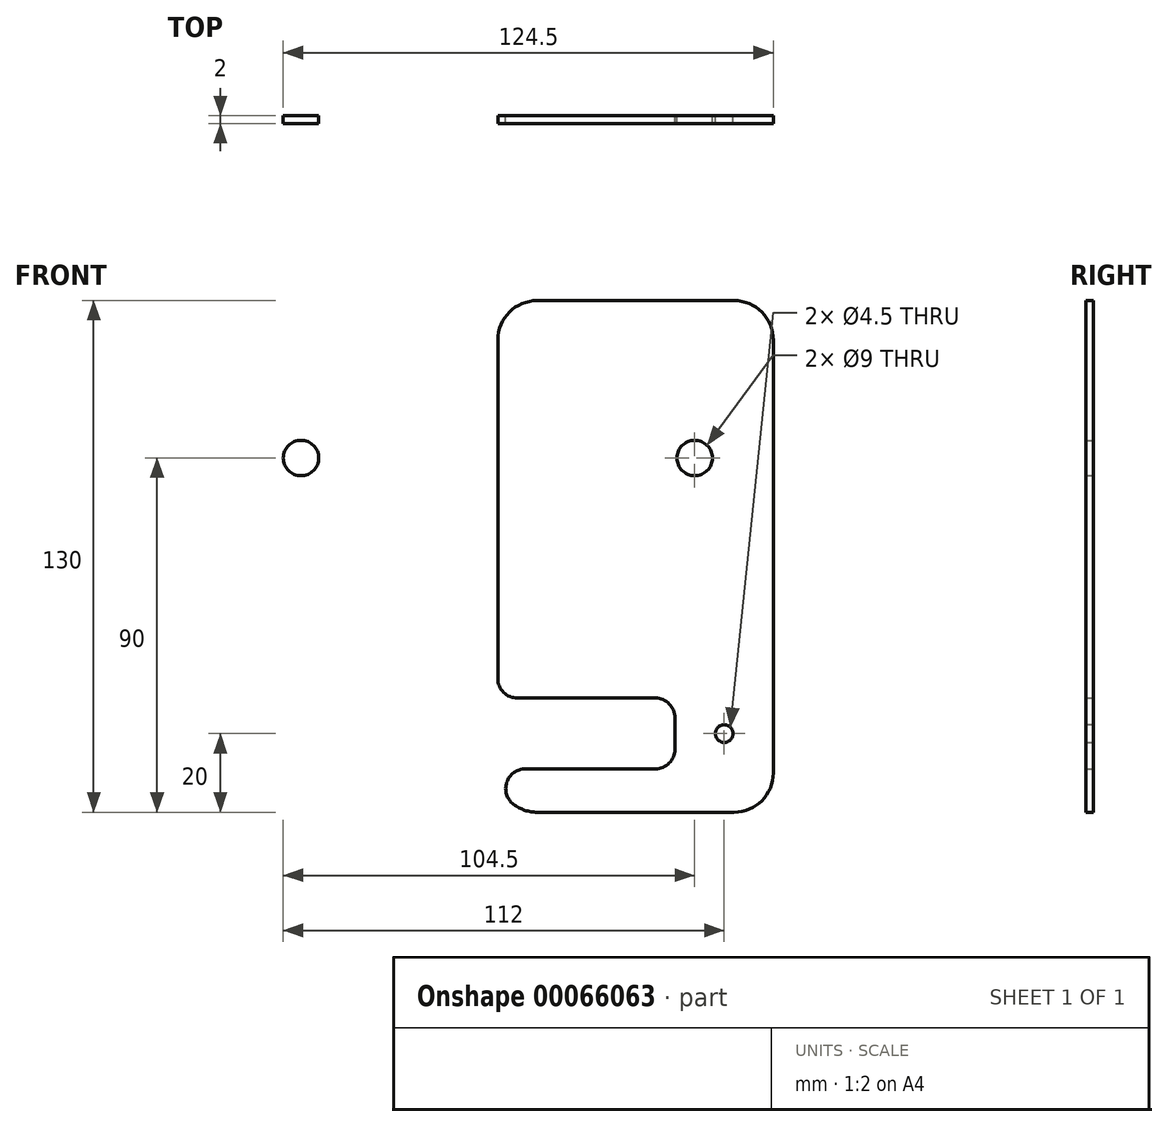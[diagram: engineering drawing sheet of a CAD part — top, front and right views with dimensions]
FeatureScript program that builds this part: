
annotation { "Feature Type Name" : "Feature", "Feature Type Description" : "" }
export const myFeature = defineFeature(function(context is Context, id is Id, definition is map)
    precondition{}
    {
        {
            var Q0;
            Q0=qCreatedBy(makeId("Front.planeOp"),FACE);
            var sketch = newSketch(context, id + "F0", { "sketchPlane" : qUnion([Q0])});
            skLineSegment(sketch, "E0.bottom", {"start": v(0, 40) * mm, "end": v(70, 40) * mm});
            skLineSegment(sketch, "E0.top", {"start": v(0, -90) * mm, "end": v(70, -90) * mm});
            skLineSegment(sketch, "E0.left", {"start": v(0, 40) * mm, "end": v(0, -90) * mm});
            skLineSegment(sketch, "E0.right", {"start": v(70, 40) * mm, "end": v(70, -90) * mm});
            skCircle(sketch, "E1", {"center": v(50, 0) * mm, "radius": 4.5 * mm});
            skLineSegment(sketch, "E2", {"start": v(0, 40) * mm, "end": v(0, -90) * mm, "construction": true});
            skCircle(sketch, "E3.0.MirrorC", {"center": v(-50, 0) * mm, "radius": 4.5 * mm});
            skCircle(sketch, "E4", {"center": v(57.5, -70) * mm, "radius": 2.25 * mm});
            skLineSegment(sketch, "E5.0.MirrorCS", {"start": v(0, 40) * mm, "end": v(-70, 40) * mm});
            skLineSegment(sketch, "E6.0.MirrorCS", {"start": v(-70, 40) * mm, "end": v(-70, -90) * mm});
            skLineSegment(sketch, "E7.0.MirrorCS", {"start": v(0, -90) * mm, "end": v(-70, -90) * mm});
            skCircle(sketch, "E8.0.MirrorC", {"center": v(-57.5, -70) * mm, "radius": 2.25 * mm});
            skLineSegment(sketch, "E9", {"start": v(0, -79) * mm, "end": v(45, -79) * mm});
            skLineSegment(sketch, "E10", {"start": v(45, -79) * mm, "end": v(45, -61) * mm});
            skLineSegment(sketch, "E11", {"start": v(45, -61) * mm, "end": v(0, -61) * mm});
            skLineSegment(sketch, "E12.0.MirrorCS", {"start": v(-45, -61) * mm, "end": v(0, -61) * mm});
            skLineSegment(sketch, "E13.0.MirrorCS", {"start": v(0, -79) * mm, "end": v(-45, -79) * mm});
            skLineSegment(sketch, "E14.0.MirrorCS", {"start": v(-45, -79) * mm, "end": v(-45, -61) * mm});
            skLineSegment(sketch, "E15", {"start": v(57.5, -70) * mm, "end": v(-57.5, -70) * mm, "construction": true});
            skLineSegment(sketch, "E16", {"start": v(70, -50) * mm, "end": v(-70, -50) * mm, "construction": true});
            skSolve(sketch);
        }
        {
            var Q0;
            Q0=makeQuery(id+"F0.imprint","IMPRINT",FACE,{"disambiguationData":[TD([[makeQuery(id+"F0.imprint","IMPRINT",EDGE,{"derivedFrom":sQuery(id+"F0.wireOp",EDGE,"E0.bottom")}),-1.0]])]});
            var Q1;
            Q1=makeQuery(id+"F0.imprint","IMPRINT",FACE,{"disambiguationData":[TD([[makeQuery(id+"F0.imprint","IMPRINT",EDGE,{"derivedFrom":sQuery(id+"F0.wireOp",EDGE,"E3.0.MirrorC")}),1.0]])]});
            extrude(context, id + "F1", {"entities" : qUnion([Q0, Q1]), "depth" : 2 * mm});
        }
        {
            var Q0;
            Q0=makeQuery(id+"F1.opExtrude","SWEPT_EDGE",EDGE,{"disambiguationData":[OSD([sQuery(id+"F0.wireOp",EDGE,"E0.bottom"),sQuery(id+"F0.wireOp",EDGE,"E0.right")])]});
            var Q1;
            Q1=makeQuery(id+"F1.opExtrude","SWEPT_EDGE",EDGE,{"disambiguationData":[OSD([sQuery(id+"F0.wireOp",EDGE,"E5.0.MirrorCS"),sQuery(id+"F0.wireOp",EDGE,"E6.0.MirrorCS")])]});
            var Q2;
            Q2=makeQuery(id+"F1.opExtrude","SWEPT_EDGE",EDGE,{"disambiguationData":[OSD([sQuery(id+"F0.wireOp",EDGE,"E0.top"),sQuery(id+"F0.wireOp",EDGE,"E0.right")])]});
            var Q3;
            Q3=makeQuery(id+"F1.opExtrude","SWEPT_EDGE",EDGE,{"disambiguationData":[OSD([sQuery(id+"F0.wireOp",EDGE,"E6.0.MirrorCS"),sQuery(id+"F0.wireOp",EDGE,"E7.0.MirrorCS")])]});
            fillet(context, id + "F2", {"entities" : qUnion([Q0, Q1, Q2, Q3]), "radius" : 10 * mm, "tangentPropagation" : true, "allowEdgeOverflow" : false});
        }
        {
            var Q0;
            Q0=makeQuery(id+"F1.opExtrude","SWEPT_EDGE",EDGE,{"disambiguationData":[OSD([sQuery(id+"F0.wireOp",EDGE,"E10"),sQuery(id+"F0.wireOp",EDGE,"E11")])]});
            var Q1;
            Q1=makeQuery(id+"F1.opExtrude","SWEPT_EDGE",EDGE,{"disambiguationData":[OSD([sQuery(id+"F0.wireOp",EDGE,"E9"),sQuery(id+"F0.wireOp",EDGE,"E10")])]});
            var Q2;
            Q2=makeQuery(id+"F1.opExtrude","SWEPT_EDGE",EDGE,{"disambiguationData":[OSD([sQuery(id+"F0.wireOp",EDGE,"E13.0.MirrorCS"),sQuery(id+"F0.wireOp",EDGE,"E14.0.MirrorCS")])]});
            var Q3;
            Q3=makeQuery(id+"F1.opExtrude","SWEPT_EDGE",EDGE,{"disambiguationData":[OSD([sQuery(id+"F0.wireOp",EDGE,"E12.0.MirrorCS"),sQuery(id+"F0.wireOp",EDGE,"E14.0.MirrorCS")])]});
            fillet(context, id + "F3", {"entities" : qUnion([Q0, Q1, Q2, Q3]), "radius" : 5 * mm, "tangentPropagation" : true, "allowEdgeOverflow" : false});
        }
    });
